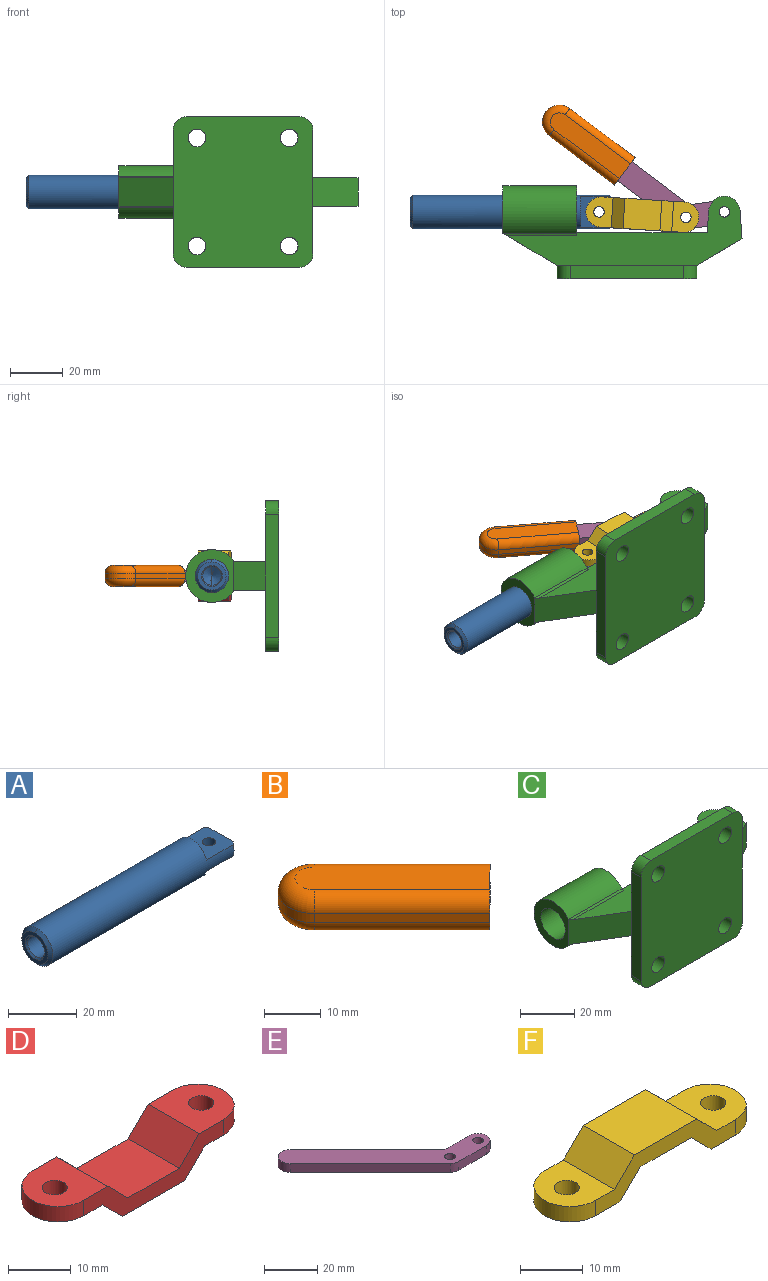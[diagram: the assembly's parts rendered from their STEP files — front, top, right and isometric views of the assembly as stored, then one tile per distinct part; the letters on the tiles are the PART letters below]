
ASSEMBLY  parts=6 mates=7
PART A: 17 faces, bbox 76.7x12.7x12.7 mm
  f0: cone r=0mm half-angle=59deg, axis (-1,0,0), area 22.4mm2, adj f4,f13
  f1: cone r=6.35mm half-angle=45deg, axis (1,0,0), area 26mm2, adj f3,f11,f14
  f2: cone r=3.49mm half-angle=45deg, axis (-1,0,0), area 8.3mm2, adj f4,f10,f14
  f3: cylinder r=6.35mm len=74.7mm, axis (1,0,0), area 2631mm2, adj f1,f6,f7,f8,f9,f11,f12,f15
  f4: cylinder r=3.49mm len=39.5mm, axis (1,0,0), area 866.8mm2, adj f0,f2,f10,f13
  f5: cylinder r=2mm len=4mm, axis (0,0,-1), area 50.3mm2, adj f6,f8
  f6: plane 12.05x12mm, normal (0,0,-1), area 131mm2, adj f3,f5,f7,f12,f15,f16
  f7: plane 12.05x4.35mm, normal (1,0,0), area 38.4mm2, adj f3,f6
  f8: plane 12.05x12mm, normal (0,0,1), area 131mm2, adj f3,f5,f9,f12,f15,f16
  f9: plane 12.05x4.35mm, normal (1,0,0), area 38.4mm2, adj f3,f8
  f10: cone r=3.49mm half-angle=45deg, axis (-1,0,0), area 8.3mm2, adj f2,f4,f14
  f11: cone r=6.35mm half-angle=45deg, axis (1,0,0), area 26mm2, adj f1,f3,f14
  f12: cone r=6.35mm half-angle=45deg, axis (-1,0,0), area 5.8mm2, adj f3,f6,f8,f16
  f13: cone r=0mm half-angle=59deg, axis (-1,0,0), area 22.4mm2, adj f0,f4
  f14: plane 10.7x10.7mm, normal (-1,0,0), area 39.8mm2, adj f1,f2,f10,f11
  f15: cone r=6.35mm half-angle=45deg, axis (-1,0,0), area 5.8mm2, adj f3,f6,f8,f16
  f16: plane 10.7x4mm, normal (1,0,0), area 41.8mm2, adj f6,f8,f12,f15
PART B: 17 faces, bbox 33.6x33.6x8 mm
  f0: cylinder r=6.5mm len=11.1mm, axis (0,0,-1), area 40.8mm2, adj f3,f6,f14,f15
  f1: cylinder r=4.5mm len=7.68mm, axis (0,0,-1), area 56.5mm2, adj f8,f9,f10,f11
  f2: cylinder r=3mm len=24.04mm, axis (-0.71,0.71,0), area 146.1mm2, adj f3,f13,f14,f16
  f3: torus R=3.5mm, axis (0,0,-1), area 80.1mm2, adj f0,f2,f4,f13
  f4: cylinder r=3mm len=24.04mm, axis (0.71,-0.71,0), area 146.1mm2, adj f3,f13,f15,f16
  f5: cylinder r=3mm len=24.04mm, axis (0.71,-0.71,0), area 146.1mm2, adj f6,f12,f14,f16
  f6: torus R=3.5mm, axis (0,0,-1), area 80.1mm2, adj f0,f5,f7,f12
  f7: cylinder r=3mm len=24.04mm, axis (-0.71,0.71,0), area 146.1mm2, adj f6,f12,f15,f16
  f8: plane 29.6x29.6mm, normal (0,0,1), area 310.8mm2, adj f1,f10,f11,f16
  f9: plane 29.6x29.6mm, normal (0,0,-1), area 310.8mm2, adj f1,f10,f11,f16
  f10: plane 21.92x21.92mm, normal (-0.71,-0.71,0), area 124mm2, adj f1,f8,f9,f16
  f11: plane 21.92x21.92mm, normal (0.71,0.71,0), area 124mm2, adj f1,f8,f9,f16
  f12: plane 27.9x27.9mm, normal (0,0,-1), area 236.2mm2, adj f5,f6,f7,f16
  f13: plane 27.9x27.9mm, normal (0,0,1), area 236.2mm2, adj f2,f3,f4,f16
  f14: plane 21.92x21.92mm, normal (0.71,0.71,0), area 62mm2, adj f0,f2,f5,f16
  f15: plane 21.92x21.92mm, normal (-0.71,-0.71,0), area 62mm2, adj f0,f4,f7,f16
  f16: plane 9.19x9.19mm, normal (0.71,-0.71,0), area 60.3mm2, adj f2,f4,f5,f7,f8,f9,f10,f11
PART C: 35 faces, bbox 90.7x35.4x57 mm
  f0: cylinder r=2mm len=4mm, axis (0,0,-1), area 44mm2, adj f12,f15
  f1: cylinder r=2mm len=4mm, axis (0,0,-1), area 44mm2, adj f11,f16
  f2: cylinder r=3.35mm len=6.7mm, axis (0,-1,0), area 105.2mm2, adj f25,f30
  f3: cylinder r=3.35mm len=6.7mm, axis (0,-1,0), area 105.2mm2, adj f24,f25
  f4: cylinder r=3.35mm len=6.7mm, axis (0,-1,0), area 105.2mm2, adj f25,f30
  f5: cylinder r=3.35mm len=6.7mm, axis (0,-1,0), area 105.2mm2, adj f24,f25
  f6: cylinder r=10mm len=28mm, axis (1,0,0), area 1405.3mm2, adj f8,f9,f13,f14,f17
  f7: cylinder r=6.35mm len=28mm, axis (1,0,0), area 1117.2mm2, adj f13,f14
  f8: cylinder r=1mm len=27.93mm, axis (1,0,0), area 25.6mm2, adj f6,f13,f16,f17
  f9: cylinder r=1mm len=27.93mm, axis (1,0,0), area 25.6mm2, adj f6,f13,f15,f17
  f10: plane 12.5x4mm, normal (0,1,0), area 50mm2, adj f11,f12,f31,f34
  f11: plane 12.5x10mm, normal (0,0,-1), area 92.6mm2, adj f1,f10,f31,f32,f34
  f12: plane 12.5x10mm, normal (0,0,1), area 92.6mm2, adj f0,f10,f31,f33,f34
  f13: plane 20x18.87mm, normal (1,0,0), area 170.3mm2, adj f6,f7,f8,f9,f15,f16,f19
  f14: plane 20x18.02mm, normal (-1,0,0), area 171.4mm2, adj f6,f7,f17
  f15: plane 89.28x26.35mm, normal (0,0,-1), area 1034.2mm2, adj f0,f9,f13,f17,f18,f19,f24,f31
  f16: plane 89.28x26.35mm, normal (0,0,1), area 1034.2mm2, adj f1,f8,f13,f17,f18,f19,f30,f31
  f17: plane 20.6x12.38mm, normal (-0.52,-0.86,0), area 264.8mm2, adj f6,f8,f9,f14,f15,f16,f28
  f18: plane 17.1x11mm, normal (0.51,-0.86,0), area 218.8mm2, adj f15,f16,f26,f31
  f19: plane 49.49x11mm, normal (0,1,0), area 544.4mm2, adj f13,f15,f16,f34
  f20: cylinder r=5mm len=5mm, axis (0,1,0), area 39.3mm2, adj f25,f27,f28,f30
  f21: cylinder r=5mm len=5mm, axis (0,1,0), area 39.3mm2, adj f25,f26,f27,f30
  f22: cylinder r=5mm len=5mm, axis (0,1,0), area 39.3mm2, adj f24,f25,f26,f29
  f23: cylinder r=5mm len=5mm, axis (0,1,0), area 39.3mm2, adj f24,f25,f28,f29
  f24: plane 53x23mm, normal (0,1,0), area 1137.8mm2, adj f3,f5,f15,f22,f23,f26,f28,f29
  f25: plane 57x53mm, normal (0,-1,0), area 2858.5mm2, adj f2,f3,f4,f5,f20,f21,f22,f23
  f26: plane 47x5mm, normal (1,0,0), area 235mm2, adj f18,f21,f22,f24,f25,f30
  f27: plane 43x5mm, normal (0,0,1), area 215mm2, adj f20,f21,f25,f30
  f28: plane 47x5mm, normal (-1,0,0), area 235mm2, adj f17,f20,f23,f24,f25,f30
  f29: plane 43x5mm, normal (0,0,-1), area 215mm2, adj f22,f23,f24,f25
  f30: plane 53x23mm, normal (0,1,0), area 1137.8mm2, adj f2,f4,f16,f20,f21,f26,f27,f28
  f31: plane 11x10.65mm, normal (1,0.07,0), area 99.5mm2, adj f10,f11,f12,f15,f16,f18,f32,f33
  f32: cylinder r=5.95mm len=11.88mm, axis (0,0,-1), area 62.6mm2, adj f11,f16,f31,f34
  f33: cylinder r=5.95mm len=11.88mm, axis (0,0,-1), area 62.6mm2, adj f12,f15,f31,f34
  f34: plane 11x8.32mm, normal (-1,0.07,0), area 73.8mm2, adj f10,f11,f12,f15,f16,f19,f32,f33
PART D: 16 faces, bbox 43x11.5x7.5 mm
  f0: cylinder r=5.75mm len=11.5mm, axis (0,0,1), area 54.2mm2, adj f4,f5,f12,f13
  f1: cylinder r=2mm len=4mm, axis (0,0,1), area 37.7mm2, adj f12,f13
  f2: cylinder r=2mm len=4mm, axis (0,0,1), area 37.7mm2, adj f7,f8
  f3: cylinder r=5.75mm len=11.5mm, axis (0,0,1), area 54.2mm2, adj f4,f5,f7,f8
  f4: plane 31.5x7.5mm, normal (0,1,0), area 105.7mm2, adj f0,f3,f6,f7,f8,f9,f10,f11
  f5: plane 31.5x7.5mm, normal (0,-1,0), area 105.7mm2, adj f0,f3,f6,f7,f8,f9,f10,f11
  f6: plane 11.5x4.5mm, normal (0.71,0,-0.71), area 73.2mm2, adj f4,f5,f7,f15
  f7: plane 11.5x10mm, normal (0,0,-1), area 88.2mm2, adj f2,f3,f4,f5,f6
  f8: plane 11.5x11.24mm, normal (0,0,1), area 102.5mm2, adj f2,f3,f4,f5,f9
  f9: plane 11.5x4.5mm, normal (-0.71,0,0.71), area 73.2mm2, adj f4,f5,f8,f10
  f10: plane 11.51x11.5mm, normal (0,0,1), area 132.4mm2, adj f4,f5,f9,f11
  f11: plane 11.5x4.5mm, normal (0.71,0,0.71), area 73.2mm2, adj f4,f5,f10,f12
  f12: plane 11.5x11.24mm, normal (0,0,1), area 102.5mm2, adj f0,f1,f4,f5,f11
  f13: plane 11.5x10mm, normal (0,0,-1), area 88.2mm2, adj f0,f1,f4,f5,f14
  f14: plane 11.5x4.5mm, normal (-0.71,0,-0.71), area 73.2mm2, adj f4,f5,f13,f15
  f15: plane 14x11.5mm, normal (0,0,-1), area 161mm2, adj f4,f5,f6,f14
PART E: 12 faces, bbox 66.2x51.4x4 mm
  f0: cylinder r=4.5mm len=9mm, axis (0,0,-1), area 56.5mm2, adj f4,f5,f7,f8
  f1: cylinder r=4.5mm len=7.68mm, axis (0,0,-1), area 56.5mm2, adj f4,f5,f10,f11
  f2: cylinder r=2mm len=4mm, axis (0,0,-1), area 50.3mm2, adj f4,f5
  f3: cylinder r=2mm len=4mm, axis (0,0,-1), area 50.3mm2, adj f4,f5
  f4: plane 66.2x51.43mm, normal (0,0,-1), area 711.2mm2, adj f0,f1,f2,f3,f6,f7,f8,f9
  f5: plane 66.2x51.43mm, normal (0,0,1), area 711.2mm2, adj f0,f1,f2,f3,f6,f7,f8,f9
  f6: cylinder r=4.5mm len=4mm, axis (0,0,-1), area 14.1mm2, adj f4,f5,f7,f11
  f7: plane 14.78x4mm, normal (0,-1,0), area 59.1mm2, adj f0,f4,f5,f6
  f8: plane 11.67x4mm, normal (0,1,0), area 46.7mm2, adj f0,f4,f5,f9
  f9: cylinder r=3mm len=4mm, axis (0,0,-1), area 9.4mm2, adj f4,f5,f8,f10
  f10: plane 40.23x40.23mm, normal (0.71,0.71,0), area 227.6mm2, adj f1,f4,f5,f9
  f11: plane 42.43x42.43mm, normal (-0.71,-0.71,0), area 240mm2, adj f1,f4,f5,f6
PART F: 16 faces, bbox 43x11.5x7.5 mm
  f0: cylinder r=5.75mm len=11.5mm, axis (0,0,-1), area 54.2mm2, adj f4,f5,f7,f8
  f1: cylinder r=2mm len=4mm, axis (0,0,-1), area 37.7mm2, adj f12,f13
  f2: cylinder r=2mm len=4mm, axis (0,0,-1), area 37.7mm2, adj f7,f8
  f3: cylinder r=5.75mm len=11.5mm, axis (0,0,-1), area 54.2mm2, adj f4,f5,f12,f13
  f4: plane 31.5x7.5mm, normal (0,-1,0), area 105.7mm2, adj f0,f3,f6,f7,f8,f9,f10,f11
  f5: plane 31.5x7.5mm, normal (0,1,0), area 105.7mm2, adj f0,f3,f6,f7,f8,f9,f10,f11
  f6: plane 11.5x4.5mm, normal (0.71,0,0.71), area 73.2mm2, adj f4,f5,f7,f15
  f7: plane 11.5x10mm, normal (0,0,1), area 88.2mm2, adj f0,f2,f4,f5,f6
  f8: plane 11.5x11.24mm, normal (0,0,-1), area 102.5mm2, adj f0,f2,f4,f5,f9
  f9: plane 11.5x4.5mm, normal (-0.71,0,-0.71), area 73.2mm2, adj f4,f5,f8,f10
  f10: plane 11.51x11.5mm, normal (0,0,-1), area 132.4mm2, adj f4,f5,f9,f11
  f11: plane 11.5x4.5mm, normal (0.71,0,-0.71), area 73.2mm2, adj f4,f5,f10,f12
  f12: plane 11.5x11.24mm, normal (0,0,-1), area 102.5mm2, adj f1,f3,f4,f5,f11
  f13: plane 11.5x10mm, normal (0,0,1), area 88.2mm2, adj f1,f3,f4,f5,f14
  f14: plane 11.5x4.5mm, normal (-0.71,0,0.71), area 73.2mm2, adj f4,f5,f13,f15
  f15: plane 14x11.5mm, normal (0,0,1), area 161mm2, adj f4,f5,f6,f14
PLACE A t=(9.38,-39.11,16.85)mm
PLACE B rot(axis=(0,0,1),8deg) t=(12.38,-44.19,16.85)mm
PLACE C t=(9.18,-39.11,16.85)mm fixed
PLACE D rot(axis=(0,0,-1),3.6deg) t=(8.09,-39.68,16.85)mm
PLACE E rot(axis=(0,0,1),8deg) t=(12.38,-44.19,16.85)mm
PLACE F rot(axis=(0,0,-1),3.6deg) t=(8.09,-39.68,16.85)mm
MATE revolute E.f2 <-> F.f2  axis (0,0,1) through (32.46,-20.76,18.85)mm
MATE fastened B.f0 <-> E.f1  axis (0,0,-1) through (-15.46,15.35,14.85)mm
MATE revolute A.f5 <-> F.f1  axis (0,0,1) through (-0.48,-18.71,18.85)mm
MATE revolute D.f1 <-> A.f5  axis (0,0,1) through (-0.48,-18.71,14.85)mm
MATE revolute D.f2 <-> E.f2  axis (0,0,1) through (32.46,-20.76,14.85)mm
MATE slider A.f3 <-> C.f7  axis (1,0,0) through (-33.83,-18.71,16.85)mm
MATE revolute E.f0 <-> C.f0  axis (0,0,1) through (47.09,-18.71,18.85)mm
